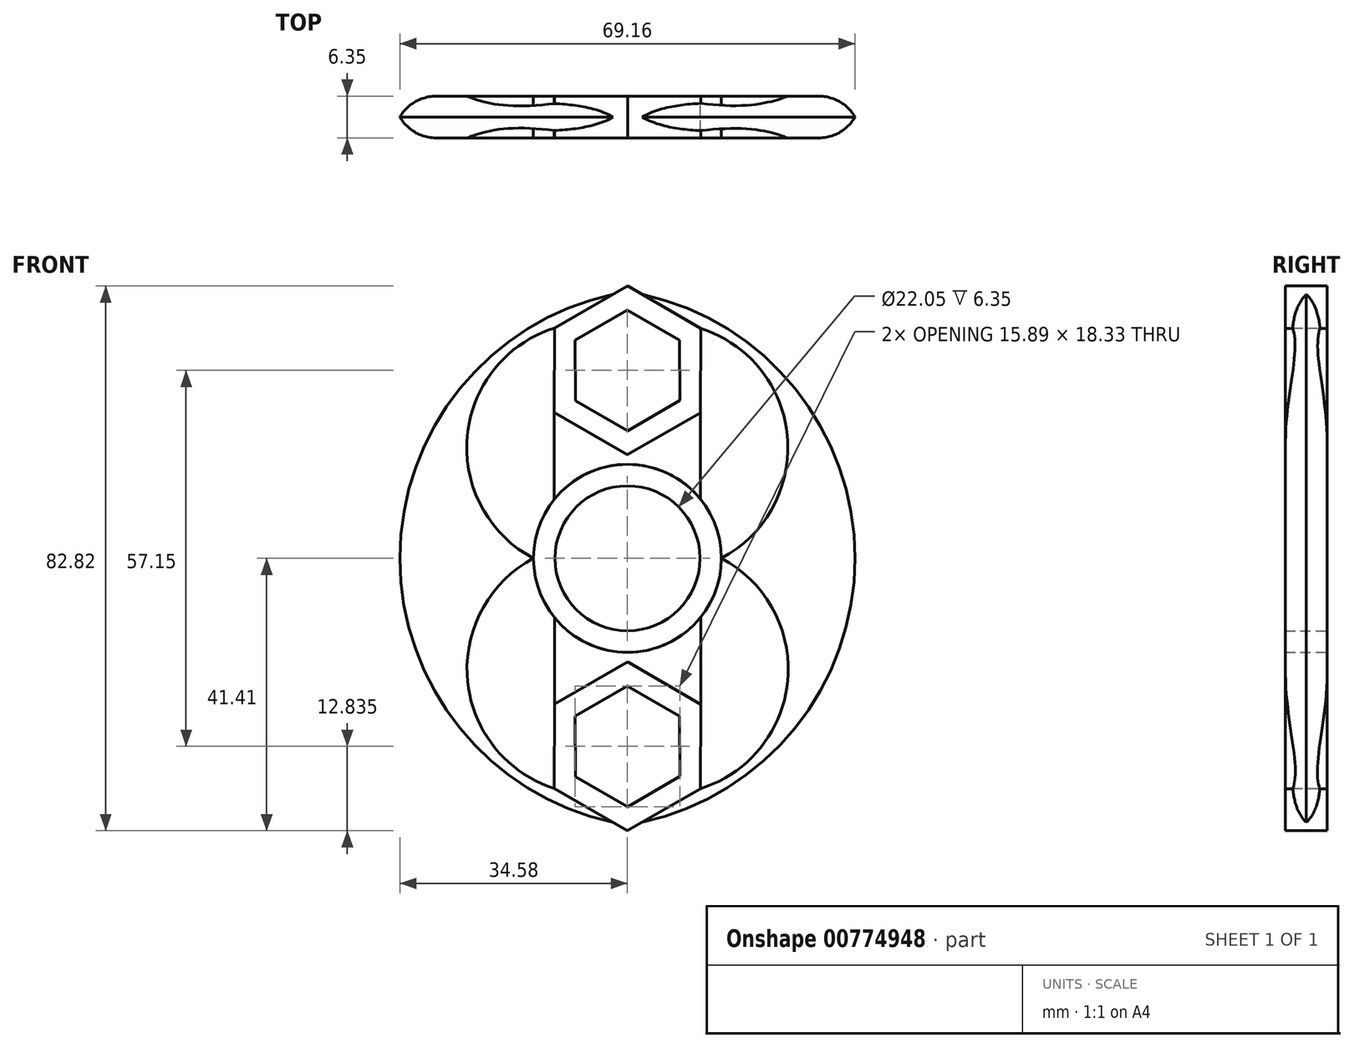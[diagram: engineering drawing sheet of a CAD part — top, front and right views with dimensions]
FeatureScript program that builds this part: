
annotation { "Feature Type Name" : "Feature", "Feature Type Description" : "" }
export const myFeature = defineFeature(function(context is Context, id is Id, definition is map)
    precondition{}
    {
        {
            var Q0;
            Q0=qCreatedBy(makeId("Front.planeOp"),FACE);
            var sketch = newSketch(context, id + "F0", { "sketchPlane" : qUnion([Q0])});
            skCircle(sketch, "E0", {"center": v(0, 0) * mm, "radius": 14.29 * mm});
            skCircle(sketch, "E1", {"center": v(0, 0) * mm, "radius": 11.02 * mm});
            skCircle(sketch, "E2.cCircle", {"center": v(0, 28.58) * mm, "radius": 11.11 * mm, "construction": true});
            skLineSegment(sketch, "E2.0", {"start": v(11.1, 22.13) * mm, "end": v(-0.03, 15.74) * mm});
            skLineSegment(sketch, "E2.1", {"start": v(-0.03, 15.74) * mm, "end": v(-11.13, 22.18) * mm});
            skLineSegment(sketch, "E2.2", {"start": v(-11.13, 22.18) * mm, "end": v(-11.1, 35.02) * mm});
            skLineSegment(sketch, "E2.3", {"start": v(-11.1, 35.02) * mm, "end": v(0.03, 41.4) * mm});
            skLineSegment(sketch, "E2.4", {"start": v(0.03, 41.4) * mm, "end": v(11.13, 34.97) * mm});
            skLineSegment(sketch, "E2.5", {"start": v(11.13, 34.97) * mm, "end": v(11.1, 22.13) * mm});
            skPoint(sketch, "E2.0.midPoint", {"position": v(5.53, 18.94) * mm});
            skCircle(sketch, "E3.cCircle", {"center": v(0, 28.58) * mm, "radius": 7.94 * mm, "construction": true});
            skLineSegment(sketch, "E3.0", {"start": v(0.01, 19.4) * mm, "end": v(-7.93, 23.98) * mm});
            skLineSegment(sketch, "E3.1", {"start": v(-7.93, 23.98) * mm, "end": v(-7.94, 33.15) * mm});
            skLineSegment(sketch, "E3.2", {"start": v(-7.94, 33.15) * mm, "end": v(-0.01, 37.74) * mm});
            skLineSegment(sketch, "E3.3", {"start": v(-0.01, 37.74) * mm, "end": v(7.93, 33.17) * mm});
            skLineSegment(sketch, "E3.4", {"start": v(7.93, 33.17) * mm, "end": v(7.94, 24) * mm});
            skLineSegment(sketch, "E3.5", {"start": v(7.94, 24) * mm, "end": v(0.01, 19.4) * mm});
            skPoint(sketch, "E3.0.midPoint", {"position": v(-3.96, 21.7) * mm});
            skLineSegment(sketch, "E4.1.0", {"start": v(-11.13, -34.97) * mm, "end": v(-11.1, -22.13) * mm});
            skPoint(sketch, "E4.1.1", {"position": v(-5.53, -18.94) * mm});
            skLineSegment(sketch, "E4.1.2", {"start": v(11.13, -22.18) * mm, "end": v(11.1, -35.02) * mm});
            skLineSegment(sketch, "E4.1.3", {"start": v(-7.94, -24) * mm, "end": v(-0.01, -19.4) * mm});
            skLineSegment(sketch, "E4.1.4", {"start": v(7.93, -23.98) * mm, "end": v(7.94, -33.15) * mm});
            skLineSegment(sketch, "E4.1.5", {"start": v(-0.01, -19.4) * mm, "end": v(7.93, -23.98) * mm});
            skCircle(sketch, "E4.1.6", {"center": v(0, -28.58) * mm, "radius": 7.94 * mm, "construction": true});
            skLineSegment(sketch, "E4.1.7", {"start": v(-7.93, -33.17) * mm, "end": v(-7.94, -24) * mm});
            skLineSegment(sketch, "E4.1.8", {"start": v(-0.03, -41.4) * mm, "end": v(-11.13, -34.97) * mm});
            skLineSegment(sketch, "E4.1.9", {"start": v(11.1, -35.02) * mm, "end": v(-0.03, -41.4) * mm});
            skLineSegment(sketch, "E4.1.10", {"start": v(-11.1, -22.13) * mm, "end": v(0.03, -15.74) * mm});
            skPoint(sketch, "E4.1.11", {"position": v(3.96, -21.7) * mm});
            skLineSegment(sketch, "E4.1.12", {"start": v(0.03, -15.74) * mm, "end": v(11.13, -22.18) * mm});
            skCircle(sketch, "E4.1.13", {"center": v(0, -28.58) * mm, "radius": 11.11 * mm, "construction": true});
            skLineSegment(sketch, "E4.1.14", {"start": v(7.94, -33.15) * mm, "end": v(0.01, -37.74) * mm});
            skLineSegment(sketch, "E4.1.15", {"start": v(0.01, -37.74) * mm, "end": v(-7.93, -33.17) * mm});
            skSolve(sketch);
        }
        {
            var Q0;
            Q0=qCreatedBy(makeId("Front.planeOp"),FACE);
            var sketch = newSketch(context, id + "F1", { "sketchPlane" : qUnion([Q0])});
            skLineSegment(sketch, "E5.0", {"start": v(7.94, -33.15) * mm, "end": v(0.01, -37.74) * mm});
            skLineSegment(sketch, "E5.1", {"start": v(0.03, -15.74) * mm, "end": v(11.13, -22.18) * mm});
            skLineSegment(sketch, "E5.2", {"start": v(11.1, 22.13) * mm, "end": v(-0.03, 15.74) * mm});
            skCircle(sketch, "E5.3", {"center": v(0, 0) * mm, "radius": 14.29 * mm});
            skLineSegment(sketch, "E5.4", {"start": v(11.1, -35.02) * mm, "end": v(-0.03, -41.4) * mm});
            skCircle(sketch, "E5.5", {"center": v(0, 0) * mm, "radius": 11.02 * mm});
            skCircle(sketch, "E5.6", {"center": v(0, -28.58) * mm, "radius": 7.94 * mm});
            skLineSegment(sketch, "E5.7", {"start": v(7.93, -23.98) * mm, "end": v(7.94, -33.15) * mm});
            skLineSegment(sketch, "E5.8", {"start": v(7.93, 33.17) * mm, "end": v(7.94, 24) * mm});
            skLineSegment(sketch, "E5.9", {"start": v(7.94, 24) * mm, "end": v(0.01, 19.4) * mm});
            skLineSegment(sketch, "E5.10", {"start": v(-0.01, 37.74) * mm, "end": v(7.93, 33.17) * mm});
            skLineSegment(sketch, "E5.11", {"start": v(11.13, -22.18) * mm, "end": v(11.1, -35.02) * mm});
            skCircle(sketch, "E5.12", {"center": v(0, 28.58) * mm, "radius": 11.11 * mm});
            skLineSegment(sketch, "E5.13", {"start": v(-0.03, 15.74) * mm, "end": v(-11.13, 22.18) * mm});
            skLineSegment(sketch, "E5.14", {"start": v(-11.13, 22.18) * mm, "end": v(-11.1, 35.02) * mm});
            skLineSegment(sketch, "E5.15", {"start": v(-11.1, 35.02) * mm, "end": v(0.03, 41.4) * mm});
            skLineSegment(sketch, "E5.16", {"start": v(0.03, 41.4) * mm, "end": v(11.13, 34.97) * mm});
            skLineSegment(sketch, "E5.17", {"start": v(11.13, 34.97) * mm, "end": v(11.1, 22.13) * mm});
            skCircle(sketch, "E5.18", {"center": v(0, 28.58) * mm, "radius": 7.94 * mm});
            skLineSegment(sketch, "E5.19", {"start": v(0.01, 19.4) * mm, "end": v(-7.93, 23.98) * mm});
            skLineSegment(sketch, "E5.20", {"start": v(-7.93, 23.98) * mm, "end": v(-7.94, 33.15) * mm});
            skLineSegment(sketch, "E5.21", {"start": v(-7.94, 33.15) * mm, "end": v(-0.01, 37.74) * mm});
            skCircle(sketch, "E5.22", {"center": v(0, -28.58) * mm, "radius": 11.11 * mm});
            skLineSegment(sketch, "E5.23", {"start": v(-11.1, -22.13) * mm, "end": v(0.03, -15.74) * mm});
            skLineSegment(sketch, "E5.24", {"start": v(-0.03, -41.4) * mm, "end": v(-11.13, -34.97) * mm});
            skLineSegment(sketch, "E5.25", {"start": v(-7.93, -33.17) * mm, "end": v(-7.94, -24) * mm});
            skLineSegment(sketch, "E5.26", {"start": v(-0.01, -19.4) * mm, "end": v(7.93, -23.98) * mm});
            skLineSegment(sketch, "E5.27", {"start": v(0.01, -37.74) * mm, "end": v(-7.93, -33.17) * mm});
            skLineSegment(sketch, "E5.28", {"start": v(-7.94, -24) * mm, "end": v(-0.01, -19.4) * mm});
            skLineSegment(sketch, "E5.29", {"start": v(-11.13, -34.97) * mm, "end": v(-11.1, -22.13) * mm});
            skLineSegment(sketch, "E6", {"start": v(-11.13, 22.18) * mm, "end": v(-11.12, 8.97) * mm});
            skLineSegment(sketch, "E7", {"start": v(11.13, -22.18) * mm, "end": v(11.12, -8.97) * mm});
            skLineSegment(sketch, "E8.trimOffspring", {"start": v(-11.1, -8.99) * mm, "end": v(-11.1, -22.13) * mm});
            skLineSegment(sketch, "E9.trimOffspring", {"start": v(11.1, 8.99) * mm, "end": v(11.1, 22.13) * mm});
            skArc(sketch, "E10", {"start": v(-11.1, 35.02) * mm, "mid": v(-24.36, 18.57) * mm, "end": v(-14.29, 0) * mm});
            skArc(sketch, "E11", {"start": v(-14.29, 0) * mm, "mid": v(-24.31, -18.53) * mm, "end": v(-11.13, -34.97) * mm});
            skArc(sketch, "E12", {"start": v(14.29, 0) * mm, "mid": v(24.31, 18.53) * mm, "end": v(11.13, 34.97) * mm});
            skArc(sketch, "E13", {"start": v(11.1, -35.02) * mm, "mid": v(24.36, -18.57) * mm, "end": v(14.29, 0) * mm});
            skArc(sketch, "E14", {"start": v(0.03, 41.4) * mm, "mid": v(-35.43, 0.02) * mm, "end": v(-0.03, -41.4) * mm});
            skArc(sketch, "E15", {"start": v(-0.03, -41.4) * mm, "mid": v(35.43, -0.02) * mm, "end": v(0.03, 41.4) * mm});
            skSolve(sketch);
        }
        {
            var Q0;
            Q0 = qSketchRegion(id + "F0", true);
            var Q1;
            {var subQ7=sQuery(id+"F1.wireOp",EDGE,"E10");Q1=makeQuery(id+"F1.imprint","IMPRINT",FACE,{"disambiguationData":[TD([[makeQuery(id+"F1.imprint","IMPRINT",EDGE,{"derivedFrom":subQ7}),-1.0]])]});}
            var Q2;
            {var subQ0=sQuery(id+"F1.wireOp",EDGE,"E12");Q2=makeQuery(id+"F1.imprint","IMPRINT",FACE,{"disambiguationData":[TD([[makeQuery(id+"F1.imprint","IMPRINT",EDGE,{"derivedFrom":subQ0}),-1.0]])]});}
            var Q3;
            {var subQ0=sQuery(id+"F1.wireOp",EDGE,"E6");Q3=makeQuery(id+"F1.imprint","IMPRINT",FACE,{"disambiguationData":[TD([[makeQuery(id+"F1.imprint","IMPRINT",EDGE,{"derivedFrom":subQ0}),1.0]])]});}
            var Q4;
            {var subQ4=sQuery(id+"F1.wireOp",EDGE,"E7");Q4=makeQuery(id+"F1.imprint","IMPRINT",FACE,{"disambiguationData":[TD([[makeQuery(id+"F1.imprint","IMPRINT",EDGE,{"derivedFrom":subQ4}),1.0]])]});}
            extrude(context, id + "F2", {"entities" : qUnion([Q0, Q1, Q2, Q3, Q4]), "depth" : 6.35 * mm, "offsetDistance" : 25.4 * mm});
        }
        {
            var Q0;
            Q0=makeQuery(id+"F2.opExtrude","CAP_EDGE",EDGE,{"disambiguationData":[OSD([sQuery(id+"F1.wireOp",EDGE,"E14")])],"isStart":false});
            var Q1;
            Q1=makeQuery(id+"F2.opExtrude","CAP_EDGE",EDGE,{"disambiguationData":[OSD([sQuery(id+"F1.wireOp",EDGE,"E15")])],"isStart":false});
            var Q2;
            Q2=makeQuery(id+"F2.opExtrude","CAP_EDGE",EDGE,{"disambiguationData":[OSD([sQuery(id+"F1.wireOp",EDGE,"E15")])],"isStart":true});
            var Q3;
            Q3=makeQuery(id+"F2.opExtrude","CAP_EDGE",EDGE,{"disambiguationData":[OSD([sQuery(id+"F1.wireOp",EDGE,"E14")])],"isStart":true});
            fillet(context, id + "F3", {"entities" : qUnion([Q0, Q1, Q2, Q3]), "radius" : 6.35 * mm, "tangentPropagation" : true, "allowEdgeOverflow" : false});
        }
    });
